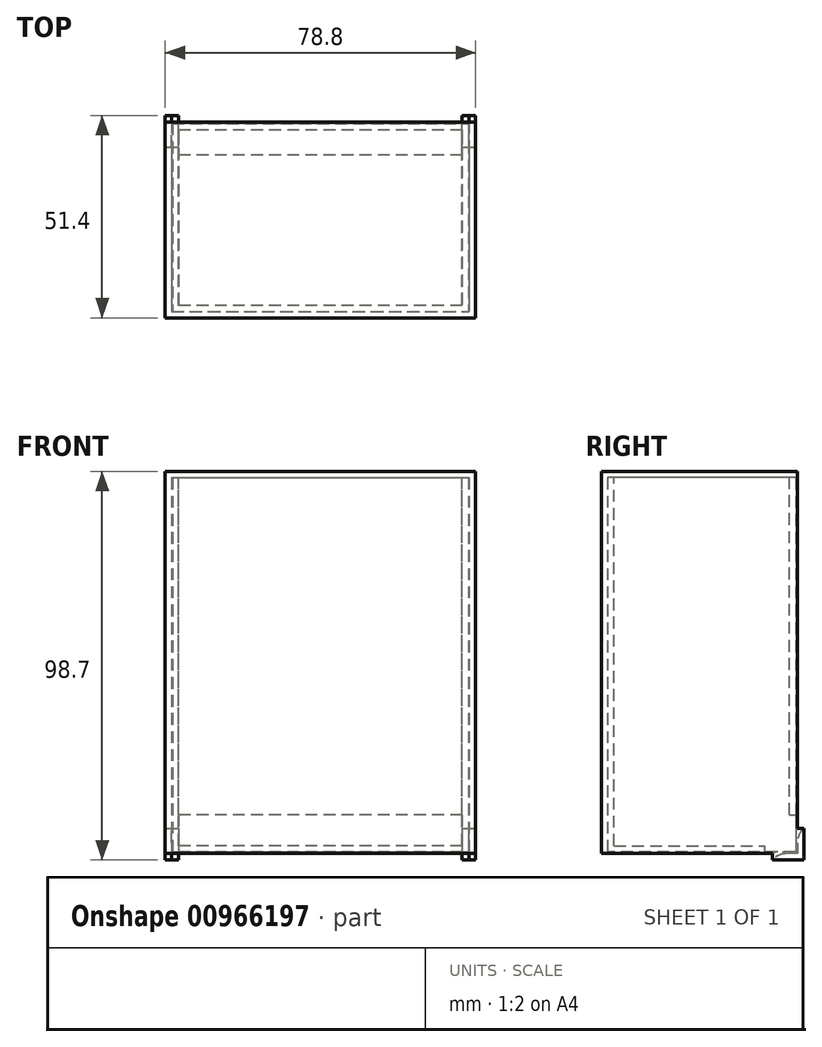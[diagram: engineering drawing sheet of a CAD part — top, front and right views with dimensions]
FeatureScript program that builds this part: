
annotation { "Feature Type Name" : "Feature", "Feature Type Description" : "" }
export const myFeature = defineFeature(function(context is Context, id is Id, definition is map)
    precondition{}
    {
        {
            var Q0;
            Q0=qCreatedBy(makeId("Front.planeOp"),FACE);
            var sketch = newSketch(context, id + "F0", { "sketchPlane" : qUnion([Q0])});
            skLineSegment(sketch, "E0.bottom", {"start": v(-33.5, 92.6) * mm, "end": v(33.5, 92.6) * mm});
            skLineSegment(sketch, "E0.top", {"start": v(-33.5, 1.6) * mm, "end": v(33.5, 1.6) * mm});
            skLineSegment(sketch, "E0.left", {"start": v(-33.5, 92.6) * mm, "end": v(-33.5, 1.6) * mm});
            skLineSegment(sketch, "E0.right", {"start": v(33.5, 92.6) * mm, "end": v(33.5, 1.6) * mm});
            skSolve(sketch);
        }
        {
            var Q0;
            Q0=qCreatedBy(makeId("Top.planeOp"),FACE);
            var sketch = newSketch(context, id + "F1", { "sketchPlane" : qUnion([Q0])});
            skLineSegment(sketch, "E1.bottom", {"start": v(-37.6, 23.9) * mm, "end": v(37.6, 23.9) * mm});
            skLineSegment(sketch, "E1.top", {"start": v(-37.6, -23.9) * mm, "end": v(37.6, -23.9) * mm});
            skLineSegment(sketch, "E1.left", {"start": v(-37.6, 23.9) * mm, "end": v(-37.6, -23.9) * mm});
            skLineSegment(sketch, "E1.right", {"start": v(37.6, 23.9) * mm, "end": v(37.6, -23.9) * mm});
            skSolve(sketch);
        }
        {
            var Q0;
            Q0=makeQuery(id+"F1.imprint","IMPRINT",FACE,{"disambiguationData":[TD([[makeQuery(id+"F1.imprint","IMPRINT",EDGE,{"derivedFrom":sQuery(id+"F1.wireOp",EDGE,"E1.bottom")}),-1.0]])]});
            var Q1;
            Q1=sQuery(id+"F0.wireOp",VERTEX,"E0.bottom.start");
            extrude(context, id + "F2", {"entities" : qUnion([Q0]), "endBound" : BoundingType.UP_TO_VERTEX, "depth" : 79.3 * mm, "endBoundEntityVertex" : qUnion([Q1]), "hasOffset" : true, "offsetDistance" : 2.5 * mm, "offsetOppositeDirection" : true});
        }
        {
            var Q0;
            Q0=makeQuery(id+"F2.opExtrude","CAP_FACE",FACE,{"disambiguationData":[OSD([sQuery(id+"F1.wireOp",EDGE,"E1.bottom"),sQuery(id+"F1.wireOp",EDGE,"E1.top"),sQuery(id+"F1.wireOp",EDGE,"E1.left"),sQuery(id+"F1.wireOp",EDGE,"E1.right")])],"isStart":false});
            var sketch = newSketch(context, id + "F3", { "sketchPlane" : qUnion([Q0])});
            skLineSegment(sketch, "E2.bottom", {"start": v(-36, 22.3) * mm, "end": v(36, 22.3) * mm});
            skLineSegment(sketch, "E2.top", {"start": v(-36, -22.3) * mm, "end": v(36, -22.3) * mm});
            skLineSegment(sketch, "E2.left", {"start": v(-36, 22.3) * mm, "end": v(-36, -22.3) * mm});
            skLineSegment(sketch, "E2.right", {"start": v(36, 22.3) * mm, "end": v(36, -22.3) * mm});
            skSolve(sketch);
        }
        {
            var Q0;
            Q0=makeQuery(id+"F3.imprint","IMPRINT",FACE,{"disambiguationData":[TD([[makeQuery(id+"F3.imprint","IMPRINT",EDGE,{"derivedFrom":sQuery(id+"F3.wireOp",EDGE,"E2.bottom")}),-1.0]])]});
            extrude(context, id + "F4", {"entities" : qUnion([Q0]), "operationType" : NewBodyOperationType.REMOVE, "endBound" : BoundingType.UP_TO_NEXT, "oppositeDirection" : true, "depth" : 25 * mm, "hasOffset" : true, "offsetDistance" : 1.6 * mm});
        }
        {
            var Q0;
            Q0=makeQuery(id+"F2.opExtrude","SWEPT_FACE",FACE,{"disambiguationData":[OSD([sQuery(id+"F1.wireOp",EDGE,"E1.top")])]});
            var sketch = newSketch(context, id + "F5", { "sketchPlane" : qUnion([Q0])});
            skLineSegment(sketch, "E3.bottom", {"start": v(-37.8, 95.1) * mm, "end": v(37.8, 95.1) * mm});
            skLineSegment(sketch, "E3.left", {"start": v(-37.8, 95.1) * mm, "end": v(-37.8, -0.4) * mm});
            skLineSegment(sketch, "E3.right", {"start": v(37.8, 95.1) * mm, "end": v(37.8, -0.4) * mm});
            skLineSegment(sketch, "E4.top", {"start": v(39.4, 96.7) * mm, "end": v(-39.4, 96.7) * mm});
            skLineSegment(sketch, "E4.left", {"start": v(39.4, -0.4) * mm, "end": v(39.4, 96.7) * mm});
            skLineSegment(sketch, "E4.right", {"start": v(-39.4, -0.4) * mm, "end": v(-39.4, 96.7) * mm});
            skLineSegment(sketch, "E5", {"start": v(37.8, -0.4) * mm, "end": v(39.4, -0.4) * mm});
            skLineSegment(sketch, "E6", {"start": v(-39.4, -0.4) * mm, "end": v(-37.8, -0.4) * mm});
            skSolve(sketch);
        }
        {
            var Q0;
            Q0 = qSketchRegion(id + "F5", true);
            var Q1;
            Q1=makeQuery(id+"F2.opExtrude","SWEPT_FACE",FACE,{"disambiguationData":[OSD([sQuery(id+"F1.wireOp",EDGE,"E1.bottom")])]});
            extrude(context, id + "F6", {"entities" : qUnion([Q0]), "endBound" : BoundingType.UP_TO_SURFACE, "oppositeDirection" : true, "depth" : 25 * mm, "endBoundEntityFace" : qUnion([Q1]), "hasOffset" : true, "offsetDistance" : .4 * mm, "offsetOppositeDirection" : true});
        }
        {
            var Q0;
            Q0=makeQuery(id+"F6.opExtrude","CAP_FACE",FACE,{"disambiguationData":[OSD([sQuery(id+"F5.wireOp",EDGE,"E3.bottom"),sQuery(id+"F5.wireOp",EDGE,"E3.left"),sQuery(id+"F5.wireOp",EDGE,"E3.right"),sQuery(id+"F5.wireOp",EDGE,"E4.top"),sQuery(id+"F5.wireOp",EDGE,"E4.left"),sQuery(id+"F5.wireOp",EDGE,"E4.right"),sQuery(id+"F5.wireOp",EDGE,"E5"),sQuery(id+"F5.wireOp",EDGE,"E6")])],"isStart":true});
            var sketch = newSketch(context, id + "F7", { "sketchPlane" : qUnion([Q0])});
            skLineSegment(sketch, "E7.bottom", {"start": v(-39.4, 96.7) * mm, "end": v(39.4, 96.7) * mm});
            skLineSegment(sketch, "E7.top", {"start": v(-39.4, -0.4) * mm, "end": v(39.4, -0.4) * mm});
            skLineSegment(sketch, "E7.left", {"start": v(-39.4, 96.7) * mm, "end": v(-39.4, -0.4) * mm});
            skLineSegment(sketch, "E7.right", {"start": v(39.4, 96.7) * mm, "end": v(39.4, -0.4) * mm});
            skSolve(sketch);
        }
        {
            var Q0;
            Q0 = qSketchRegion(id + "F7", true);
            extrude(context, id + "F8", {"entities" : qUnion([Q0]), "operationType" : NewBodyOperationType.ADD, "depth" : 1.6 * mm, "offsetDistance" : 25 * mm});
        }
        {
            var Q0;
            Q0=makeQuery(id+"F8.boolean.opBoolean","MERGE",FACE,{"derivedFrom":[makeQuery(id+"F6.opExtrude","SWEPT_FACE",FACE,{"disambiguationData":[OSD([sQuery(id+"F5.wireOp",EDGE,"E4.left")])]}),makeQuery(id+"F8.opExtrude","SWEPT_FACE",FACE,{"disambiguationData":[OSD([sQuery(id+"F7.wireOp",EDGE,"E7.right")])]})]});
            var sketch = newSketch(context, id + "F9", { "sketchPlane" : qUnion([Q0])});
            skLineSegment(sketch, "E8.bottom", {"start": v(25.9, -2) * mm, "end": v(17.9, -2) * mm});
            skLineSegment(sketch, "E8.top", {"start": v(25.9, 6) * mm, "end": v(17.9, 6) * mm});
            skLineSegment(sketch, "E8.left", {"start": v(25.9, -2) * mm, "end": v(25.9, 6) * mm});
            skLineSegment(sketch, "E8.right", {"start": v(17.9, -2) * mm, "end": v(17.9, 6) * mm});
            skSolve(sketch);
        }
        {
            var Q0;
            {var subQ1=sQuery(id+"F9.wireOp",EDGE,"E8.bottom");Q0=makeQuery(id+"F9.imprint","IMPRINT",FACE,{"disambiguationData":[TD([[makeQuery(id+"F9.imprint","IMPRINT",EDGE,{"derivedFrom":subQ1}),-1.0]])]});}
            var Q1;
            Q1=makeQuery(id+"F8.boolean.opBoolean","MERGE",FACE,{"derivedFrom":[makeQuery(id+"F6.opExtrude","SWEPT_FACE",FACE,{"disambiguationData":[OSD([sQuery(id+"F5.wireOp",EDGE,"E4.right")])]}),makeQuery(id+"F8.opExtrude","SWEPT_FACE",FACE,{"disambiguationData":[OSD([sQuery(id+"F7.wireOp",EDGE,"E7.left")])]})]});
            extrude(context, id + "F10", {"entities" : qUnion([Q0]), "operationType" : NewBodyOperationType.ADD, "endBound" : BoundingType.UP_TO_SURFACE, "oppositeDirection" : true, "depth" : 25 * mm, "endBoundEntityFace" : qUnion([Q1]), "offsetDistance" : 25 * mm});
        }
        {
            var Q0;
            Q0=makeQuery(id+"F10.opExtrude","SWEPT_FACE",FACE,{"disambiguationData":[OSD([sQuery(id+"F9.wireOp",EDGE,"E8.left")])]});
            var sketch = newSketch(context, id + "F11", { "sketchPlane" : qUnion([Q0])});
            skLineSegment(sketch, "E9.bottom", {"start": v(-36, 9.48) * mm, "end": v(36, 9.48) * mm});
            skLineSegment(sketch, "E9.top", {"start": v(-36, -4.58) * mm, "end": v(36, -4.58) * mm});
            skLineSegment(sketch, "E9.left", {"start": v(-36, 9.48) * mm, "end": v(-36, -4.58) * mm});
            skLineSegment(sketch, "E9.right", {"start": v(36, 9.48) * mm, "end": v(36, -4.58) * mm});
            skSolve(sketch);
        }
        {
            var Q0;
            Q0 = qSketchRegion(id + "F11", true);
            extrude(context, id + "F12", {"entities" : qUnion([Q0]), "operationType" : NewBodyOperationType.REMOVE, "oppositeDirection" : true, "depth" : 10 * mm, "offsetDistance" : 25 * mm});
        }
        {
            var Q0;
            {var subQ0=makeQuery(id+"F6.opExtrude","SWEPT_FACE",FACE,{"disambiguationData":[OSD([sQuery(id+"F5.wireOp",EDGE,"E6")])]});var subQ1=sQuery(id+"F5.wireOp",EDGE,"E5");var subQ2=makeQuery(id+"F6.opExtrude","SWEPT_FACE",FACE,{"disambiguationData":[OSD([subQ1])]});var subQ3=sQuery(id+"F9.wireOp",EDGE,"E8.right");var subQ4=sQuery(id+"F7.wireOp",EDGE,"E7.right");var subQ5=sQuery(id+"F7.wireOp",EDGE,"E7.top");var subQ6=sQuery(id+"F5.wireOp",EDGE,"E4.left");var subQ7=makeQuery(id+"F8.opExtrude","SWEPT_FACE",FACE,{"disambiguationData":[OSD([subQ5])]});var subQ8=makeQuery(id+"F10.opExtrude","SWEPT_FACE",FACE,{"disambiguationData":[OSD([subQ3])]});Q0=makeQuery(id+"F10.boolean.opBoolean","SPLIT",EDGE,{"disambiguationData":[topologyDisambiguationEdgeConnected([subQ2,subQ0,subQ7,subQ8]),TD([makeQuery(id+"F6.opExtrude","SWEPT_FACE",FACE,{"disambiguationData":[OSD([sQuery(id+"F5.wireOp",EDGE,"E3.left")])]})])],"derivedFrom":makeQuery(id+"F10.opExtrude","SWEPT_EDGE",EDGE,{"disambiguationData":[OSD([subQ6,subQ1,subQ5,subQ4,subQ3])]})});}
            var Q1;
            {var subQ0=sQuery(id+"F5.wireOp",EDGE,"E5");var subQ1=makeQuery(id+"F6.opExtrude","SWEPT_FACE",FACE,{"disambiguationData":[OSD([subQ0])]});var subQ2=sQuery(id+"F5.wireOp",EDGE,"E4.left");var subQ3=sQuery(id+"F7.wireOp",EDGE,"E7.right");var subQ4=makeQuery(id+"F6.opExtrude","SWEPT_FACE",FACE,{"disambiguationData":[OSD([sQuery(id+"F5.wireOp",EDGE,"E6")])]});var subQ5=sQuery(id+"F7.wireOp",EDGE,"E7.top");var subQ6=makeQuery(id+"F8.opExtrude","SWEPT_FACE",FACE,{"disambiguationData":[OSD([subQ5])]});var subQ7=sQuery(id+"F9.wireOp",EDGE,"E8.right");var subQ8=makeQuery(id+"F10.opExtrude","SWEPT_FACE",FACE,{"disambiguationData":[OSD([subQ7])]});Q1=makeQuery(id+"F10.boolean.opBoolean","SPLIT",EDGE,{"disambiguationData":[topologyDisambiguationEdgeConnected([subQ1,subQ4,subQ6,subQ8]),TD([makeQuery(id+"F6.opExtrude","SWEPT_FACE",FACE,{"disambiguationData":[OSD([sQuery(id+"F5.wireOp",EDGE,"E3.right")])]})])],"derivedFrom":makeQuery(id+"F10.opExtrude","SWEPT_EDGE",EDGE,{"disambiguationData":[OSD([subQ2,subQ0,subQ5,subQ3,subQ7])]})});}
            var Q2;
            {var subQ0=sQuery(id+"F5.wireOp",EDGE,"E3.left");var subQ1=sQuery(id+"F5.wireOp",EDGE,"E4.right");var subQ2=sQuery(id+"F5.wireOp",EDGE,"E5");var subQ3=sQuery(id+"F5.wireOp",EDGE,"E4.left");var subQ4=makeQuery(id+"F6.opExtrude","CAP_FACE",FACE,{"disambiguationData":[OSD([sQuery(id+"F5.wireOp",EDGE,"E3.bottom"),subQ0,sQuery(id+"F5.wireOp",EDGE,"E3.right"),sQuery(id+"F5.wireOp",EDGE,"E4.top"),subQ3,subQ1,subQ2,sQuery(id+"F5.wireOp",EDGE,"E6")])],"isStart":false});var subQ5=sQuery(id+"F9.wireOp",EDGE,"E8.top");var subQ6=makeQuery(id+"F10.opExtrude","SWEPT_FACE",FACE,{"disambiguationData":[OSD([subQ5])]});Q2=makeQuery(id+"F10.boolean.opBoolean","SPLIT",EDGE,{"disambiguationData":[topologyDisambiguationEdgeConnected([subQ4,subQ6]),TD([makeQuery(id+"F6.opExtrude","SWEPT_FACE",FACE,{"disambiguationData":[OSD([subQ0])]})])],"derivedFrom":makeQuery(id+"F10.opExtrude","SWEPT_EDGE",EDGE,{"disambiguationData":[OSD([subQ3,subQ5])]})});}
            var Q3;
            {var subQ1=sQuery(id+"F5.wireOp",EDGE,"E4.left");var subQ2=sQuery(id+"F5.wireOp",EDGE,"E3.right");var subQ3=sQuery(id+"F5.wireOp",EDGE,"E5");var subQ4=makeQuery(id+"F6.opExtrude","CAP_FACE",FACE,{"disambiguationData":[OSD([sQuery(id+"F5.wireOp",EDGE,"E3.bottom"),sQuery(id+"F5.wireOp",EDGE,"E3.left"),subQ2,sQuery(id+"F5.wireOp",EDGE,"E4.top"),subQ1,sQuery(id+"F5.wireOp",EDGE,"E4.right"),subQ3,sQuery(id+"F5.wireOp",EDGE,"E6")])],"isStart":false});var subQ5=sQuery(id+"F9.wireOp",EDGE,"E8.top");var subQ6=makeQuery(id+"F10.opExtrude","SWEPT_FACE",FACE,{"disambiguationData":[OSD([subQ5])]});Q3=makeQuery(id+"F10.boolean.opBoolean","SPLIT",EDGE,{"disambiguationData":[topologyDisambiguationEdgeConnected([subQ4,subQ6]),TD([makeQuery(id+"F6.opExtrude","SWEPT_FACE",FACE,{"disambiguationData":[OSD([subQ2])]})])],"derivedFrom":makeQuery(id+"F10.opExtrude","SWEPT_EDGE",EDGE,{"disambiguationData":[OSD([subQ1,subQ5])]})});}
            fillet(context, id + "F13", {"entities" : qUnion([Q0, Q1, Q2, Q3]), "radius" : 5 * mm, "tangentPropagation" : true, "allowEdgeOverflow" : false});
        }
    });
